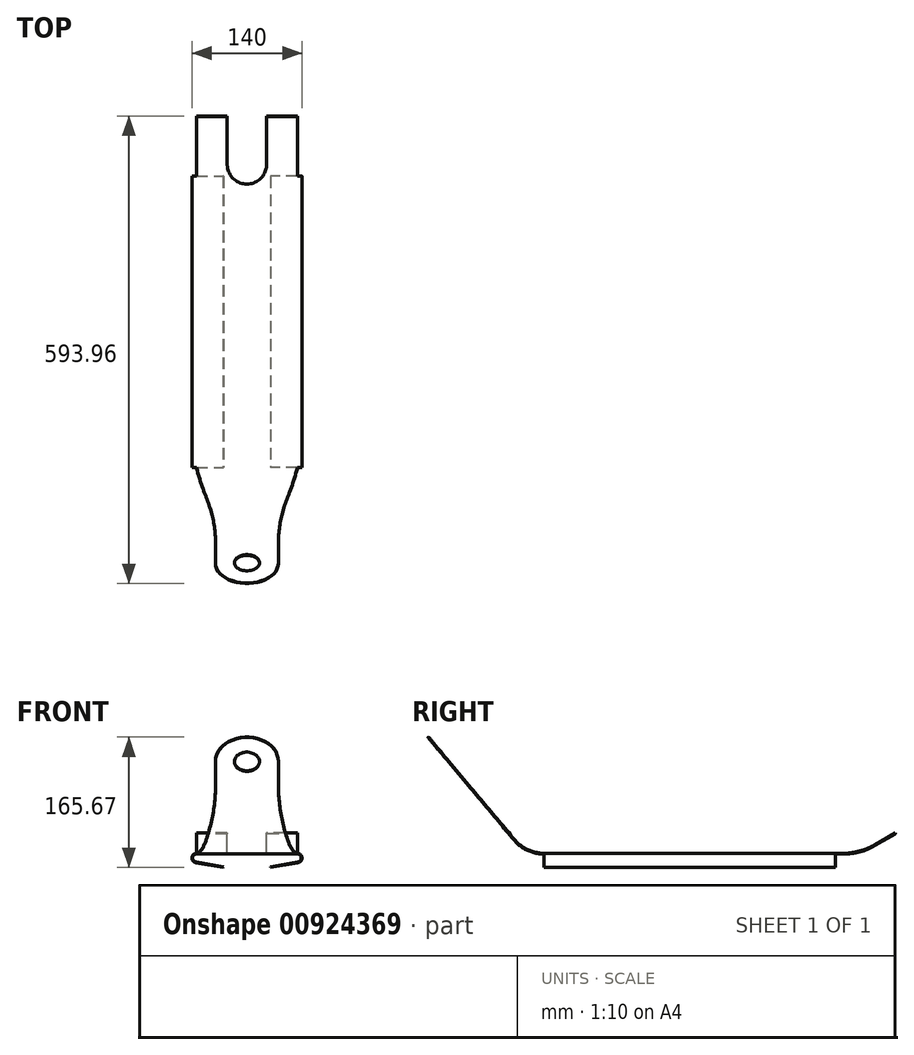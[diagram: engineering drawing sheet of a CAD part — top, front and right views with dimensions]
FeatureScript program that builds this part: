
annotation { "Feature Type Name" : "Feature", "Feature Type Description" : "" }
export const myFeature = defineFeature(function(context is Context, id is Id, definition is map)
    precondition{}
    {
        {
            var Q0;
            Q0=qCreatedBy(makeId("Right.planeOp"),FACE);
            var sketch = newSketch(context, id + "F0", { "sketchPlane" : qUnion([Q0])});
            skLineSegment(sketch, "E0", {"start": v(0, 0) * mm, "end": v(380, 0) * mm});
            skLineSegment(sketch, "E1", {"start": v(-37.54, 17.5) * mm, "end": v(-121, 116.97) * mm});
            skLineSegment(sketch, "E2", {"start": v(0, 0) * mm, "end": v(-121, 0) * mm, "construction": true});
            skLineSegment(sketch, "E3", {"start": v(-121, 0) * mm, "end": v(-121, 116.97) * mm, "construction": true});
            skLineSegment(sketch, "E4", {"start": v(-121, 116.97) * mm, "end": v(-187.18, 195.85) * mm});
            skLineSegment(sketch, "E5", {"start": v(380, 0) * mm, "end": v(420, 0) * mm, "construction": true});
            skArc(sketch, "E6", {"start": v(380, 0) * mm, "mid": v(400.7, 2.73) * mm, "end": v(420, 10.72) * mm});
            skLineSegment(sketch, "E7", {"start": v(420, 0) * mm, "end": v(420, 40.59) * mm, "construction": true});
            skPoint(sketch, "E8.visualSharp", {"position": v(-22.85, 0) * mm});
            skArc(sketch, "E8.filletArc", {"start": v(-37.54, 17.5) * mm, "mid": v(-20.7, 4.6) * mm, "end": v(0, 0) * mm});
            skLineSegment(sketch, "E9.0", {"start": v(-38.3, 16.86) * mm, "end": v(-128.37, 124.2) * mm});
            skArc(sketch, "E9.1", {"start": v(-38.3, 16.86) * mm, "mid": v(-21.13, 3.68) * mm, "end": v(0, -1) * mm});
            skLineSegment(sketch, "E9.2", {"start": v(0, -1) * mm, "end": v(380, -1) * mm});
            skArc(sketch, "E9.3", {"start": v(380, -1) * mm, "mid": v(400.96, 1.76) * mm, "end": v(420.5, 9.85) * mm});
            skLineSegment(sketch, "E10.0", {"start": v(-128.37, 124.2) * mm, "end": v(-187.84, 195.07) * mm});
            skLineSegment(sketch, "E11", {"start": v(-187.18, 195.85) * mm, "end": v(-187.84, 195.07) * mm});
            skLineSegment(sketch, "E12", {"start": v(420, 10.72) * mm, "end": v(445.98, 25.72) * mm});
            skLineSegment(sketch, "E13.0", {"start": v(420.5, 9.85) * mm, "end": v(446.48, 24.85) * mm});
            skLineSegment(sketch, "E14", {"start": v(445.98, 25.72) * mm, "end": v(446.48, 24.85) * mm});
            skSolve(sketch);
        }
        {
            var Q0;
            Q0=makeQuery(id+"F0.imprint","IMPRINT",FACE,{"disambiguationData":[TD([[makeQuery(id+"F0.imprint","IMPRINT",EDGE,{"derivedFrom":sQuery(id+"F0.wireOp",EDGE,"E0")}),-1.0]])]});
            extrude(context, id + "F1", {"entities" : qUnion([Q0]), "endBound" : BoundingType.SYMMETRIC, "depth" : 128 * mm, "offsetDistance" : 25 * mm});
        }
        {
            var Q0;
            Q0=qCreatedBy(makeId("Front.planeOp"),FACE);
            var sketch = newSketch(context, id + "F2", { "sketchPlane" : qUnion([Q0])});
            skLineSegment(sketch, "E15.0", {"start": v(64, 0) * mm, "end": v(-64, 0) * mm});
            skLineSegment(sketch, "E16.0", {"start": v(64, -1) * mm, "end": v(-64, -1) * mm});
            skArc(sketch, "E17", {"start": v(64, -1) * mm, "mid": v(68.98, -5.56) * mm, "end": v(64.87, -10.92) * mm});
            skLineSegment(sketch, "E18", {"start": v(64.87, -10.92) * mm, "end": v(29.99, -17.07) * mm});
            skLineSegment(sketch, "E19.0", {"start": v(65.04, -11.9) * mm, "end": v(30.16, -18.06) * mm});
            skArc(sketch, "E19.1", {"start": v(64, 0) * mm, "mid": v(69.98, -5.48) * mm, "end": v(65.04, -11.9) * mm});
            skLineSegment(sketch, "E20", {"start": v(29.99, -17.07) * mm, "end": v(30.16, -18.06) * mm});
            skLineSegment(sketch, "E21.MirrorCS", {"start": v(-65.04, -11.9) * mm, "end": v(-30.16, -18.06) * mm});
            skLineSegment(sketch, "E22.MirrorCS", {"start": v(-64.87, -10.92) * mm, "end": v(-29.99, -17.07) * mm});
            skArc(sketch, "E23.MirrorCS", {"start": v(-64, 0) * mm, "mid": v(-69.98, -5.48) * mm, "end": v(-65.04, -11.9) * mm});
            skArc(sketch, "E24.MirrorCS", {"start": v(-64, -1) * mm, "mid": v(-68.98, -5.56) * mm, "end": v(-64.87, -10.92) * mm});
            skLineSegment(sketch, "E25.MirrorCS", {"start": v(-29.99, -17.07) * mm, "end": v(-30.16, -18.06) * mm});
            skSolve(sketch);
        }
        {
            var Q0;
            Q0=makeQuery(id+"F2.imprint","IMPRINT",FACE,{"disambiguationData":[TD([[makeQuery(id+"F2.imprint","IMPRINT",EDGE,{"derivedFrom":sQuery(id+"F2.wireOp",EDGE,"E15.0")}),1.0]])]});
            extrude(context, id + "F3", {"entities" : qUnion([Q0]), "operationType" : NewBodyOperationType.ADD, "oppositeDirection" : true, "depth" : 370 * mm, "offsetDistance" : 25 * mm});
        }
        {
            var Q0;
            Q0=makeQuery(id+"F1.opExtrude","SWEPT_FACE",FACE,{"disambiguationData":[OSD([sQuery(id+"F0.wireOp",EDGE,"E0")])]});
            cPlane(context, id + "F4", {"entities" : qUnion([Q0]), "cplaneType" : CPlaneType.OFFSET, "offset" : 400 * mm, "width" : 150 * mm, "height" : 150 * mm});
        }
        {
            var Q0;
            Q0=qCreatedBy(id+"F4.planeOp",FACE);
            var sketch = newSketch(context, id + "F5", { "sketchPlane" : qUnion([Q0])});
            skPoint(sketch, "E26.0", {"position": v(0, 0) * mm});
            skLineSegment(sketch, "E27", {"start": v(0, 0) * mm, "end": v(0, 385) * mm, "construction": true});
            skArc(sketch, "E28", {"start": v(-25, 385) * mm, "mid": v(0, 360) * mm, "end": v(25, 385) * mm});
            skLineSegment(sketch, "E29", {"start": v(-25, 385) * mm, "end": v(-25, 446.48) * mm});
            skLineSegment(sketch, "E30.MirrorCS", {"start": v(25, 385) * mm, "end": v(25, 446.48) * mm});
            skPoint(sketch, "E31.0.end.orphan", {"position": v(-25, 448.59) * mm});
            skPoint(sketch, "E31.0.start.orphan", {"position": v(25, 448.59) * mm});
            skLineSegment(sketch, "E32.0", {"start": v(25, 446.48) * mm, "end": v(-25, 446.48) * mm});
            skSolve(sketch);
        }
        {
            var Q0;
            Q0=makeQuery(id+"F5.imprint","IMPRINT",FACE,{"disambiguationData":[TD([[makeQuery(id+"F5.imprint","IMPRINT",EDGE,{"derivedFrom":sQuery(id+"F5.wireOp",EDGE,"E28")}),1.0]])]});
            extrude(context, id + "F6", {"entities" : qUnion([Q0]), "operationType" : NewBodyOperationType.REMOVE, "oppositeDirection" : true, "depth" : 500 * mm, "offsetDistance" : 25 * mm});
        }
        {
            var Q0;
            Q0=makeQuery(id+"F1.opExtrude","SWEPT_FACE",FACE,{"disambiguationData":[OSD([sQuery(id+"F0.wireOp",EDGE,"E1"),sQuery(id+"F0.wireOp",EDGE,"E4")])]});
            cPlane(context, id + "F7", {"entities" : qUnion([Q0]), "cplaneType" : CPlaneType.OFFSET, "offset" : 500 * mm, "width" : 150 * mm, "height" : 150 * mm});
        }
        {
            var Q0;
            Q0=qCreatedBy(id+"F7.planeOp",FACE);
            var sketch = newSketch(context, id + "F8", { "sketchPlane" : qUnion([Q0])});
            skPoint(sketch, "E33.0", {"position": v(0, 167.38) * mm});
            skCircle(sketch, "E34", {"center": v(0, 167.38) * mm, "radius": 15.9 * mm});
            skCircle(sketch, "E35", {"center": v(0, 167.38) * mm, "radius": 40 * mm});
            skPoint(sketch, "E36.0", {"position": v(-64, 0) * mm});
            skPoint(sketch, "E37.0", {"position": v(64, 0) * mm});
            skPoint(sketch, "E38.0", {"position": v(64, 37.54) * mm});
            skPoint(sketch, "E39.0", {"position": v(-64, 37.54) * mm});
            skLineSegment(sketch, "E40.0.0", {"start": v(64, 37.54) * mm, "end": v(64, 270.35) * mm});
            skLineSegment(sketch, "E40.0.1", {"start": v(64, 270.35) * mm, "end": v(-64, 270.35) * mm});
            skLineSegment(sketch, "E40.0.2", {"start": v(-64, 270.35) * mm, "end": v(-64, 37.54) * mm});
            skLineSegment(sketch, "E41.0", {"start": v(-64, 37.54) * mm, "end": v(-64, 0) * mm});
            skLineSegment(sketch, "E42.0", {"start": v(64, 37.54) * mm, "end": v(64, 0) * mm});
            skLineSegment(sketch, "E43", {"start": v(0, 167.38) * mm, "end": v(-40, 167.38) * mm, "construction": true});
            skLineSegment(sketch, "E44", {"start": v(-40, 167.38) * mm, "end": v(-40, 127.38) * mm});
            skLineSegment(sketch, "E45.MirrorCS", {"start": v(40, 167.38) * mm, "end": v(40, 127.38) * mm});
            skArc(sketch, "E46", {"start": v(-64, 0) * mm, "mid": v(-46.05, 62.57) * mm, "end": v(-40, 127.38) * mm});
            skArc(sketch, "E47.MirrorCS", {"start": v(64, 0) * mm, "mid": v(46.05, 62.57) * mm, "end": v(40, 127.38) * mm});
            skSolve(sketch);
        }
        {
            var Q0;
            Q0=makeQuery(id+"F8.imprint","IMPRINT",FACE,{"disambiguationData":[TD([[makeQuery(id+"F8.imprint","IMPRINT",EDGE,{"derivedFrom":sQuery(id+"F8.wireOp",EDGE,"E34")}),1.0]])]});
            var Q1;
            {var subQ1=sQuery(id+"F8.wireOp",EDGE,"xvVkaBp2-z952-ktE2-W5i3-IFcbgTmpOrFC");Q1=makeQuery(id+"F8.imprint","IMPRINT",FACE,{"disambiguationData":[TD([[makeQuery(id+"F8.imprint","IMPRINT",EDGE,{"derivedFrom":subQ1}),-1.0]])]});}
            var Q2;
            Q2=makeQuery(id+"F8.imprint","IMPRINT",FACE,{"disambiguationData":[TD([[makeQuery(id+"F8.imprint","IMPRINT",EDGE,{"derivedFrom":sQuery(id+"F8.wireOp",EDGE,"pBGuUWYm-rugK-GzeX-ICKP-5gp0v7GJHHkn")}),-1.0]])]});
            var Q3;
            Q3=makeQuery(id+"F8.imprint","IMPRINT",FACE,{"disambiguationData":[TD([[makeQuery(id+"F8.imprint","IMPRINT",EDGE,{"derivedFrom":sQuery(id+"F8.wireOp",EDGE,"JaScSxbA-Eezx-xXKZ-oBlD-ZaHvaq5aMFxB")}),-1.0]])]});
            var Q4;
            Q4=makeQuery(id+"F8.imprint","IMPRINT",FACE,{"disambiguationData":[TD([[makeQuery(id+"F8.imprint","IMPRINT",EDGE,{"derivedFrom":sQuery(id+"F8.wireOp",EDGE,"E40.0.0")}),1.0]])]});
            extrude(context, id + "F9", {"entities" : qUnion([Q0, Q1, Q2, Q3, Q4]), "operationType" : NewBodyOperationType.REMOVE, "oppositeDirection" : true, "depth" : 600 * mm, "offsetDistance" : 25 * mm});
        }
        {
            var Q0;
            Q0=qCreatedBy(makeId("Right.planeOp"),FACE);
            cPlane(context, id + "F10", {"entities" : qUnion([Q0]), "cplaneType" : CPlaneType.OFFSET, "offset" : 400 * mm, "width" : 150 * mm, "height" : 150 * mm});
        }
        {
            var Q0;
            Q0=makeQuery(id+"F1.opExtrude","SWEPT_FACE",FACE,{"disambiguationData":[OSD([sQuery(id+"F0.wireOp",EDGE,"E9.2")])]});
            var sketch = newSketch(context, id + "F11", { "sketchPlane" : qUnion([Q0])});
            skPoint(sketch, "E48.0", {"position": v(-29.99, 0) * mm});
            skPoint(sketch, "E49.0", {"position": v(30.16, 0) * mm});
            skSolve(sketch);
        }
    });
